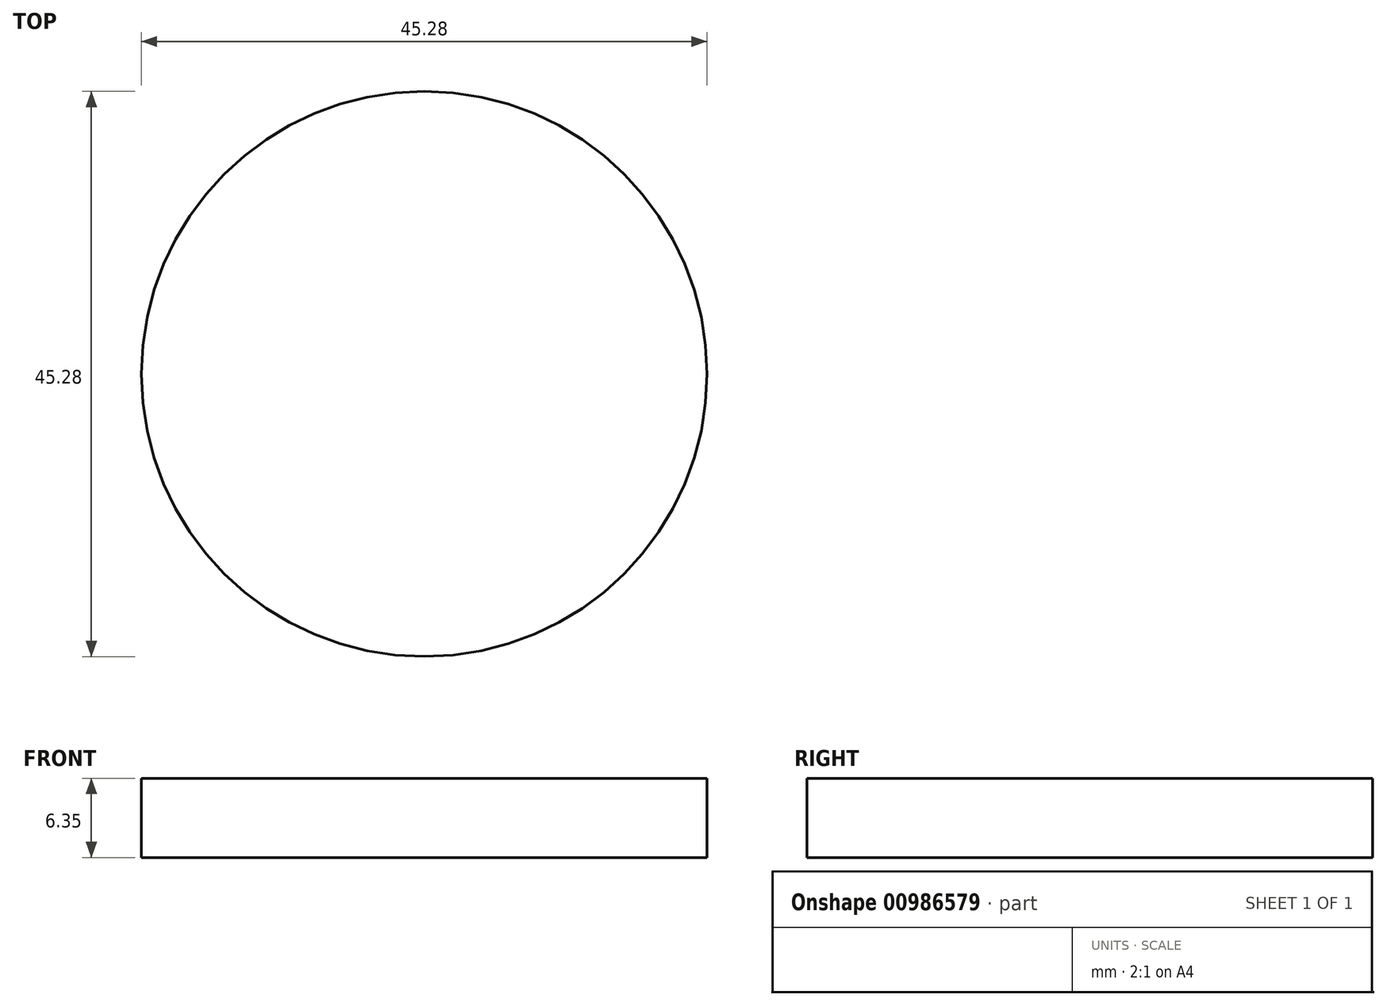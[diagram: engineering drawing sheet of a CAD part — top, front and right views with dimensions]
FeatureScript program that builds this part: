
annotation { "Feature Type Name" : "Feature", "Feature Type Description" : "" }
export const myFeature = defineFeature(function(context is Context, id is Id, definition is map)
    precondition{}
    {
        {
            var Q0;
            Q0=qCreatedBy(makeId("Top.planeOp"),FACE);
            var sketch = newSketch(context, id + "F0", { "sketchPlane" : qUnion([Q0])});
            skCircle(sketch, "E0", {"center": v(0, 0) * mm, "radius": 22.64 * mm});
            skSolve(sketch);
        }
        {
            var Q0;
            Q0=makeQuery(id+"F0.imprint","IMPRINT",FACE,{"disambiguationData":[TD([[makeQuery(id+"F0.imprint","IMPRINT",EDGE,{"derivedFrom":sQuery(id+"F0.wireOp",EDGE,"E0")}),1.0]])]});
            extrude(context, id + "F1", {"entities" : qUnion([Q0]), "depth" : 6.35 * mm, "offsetDistance" : 25.4 * mm});
        }
    });
